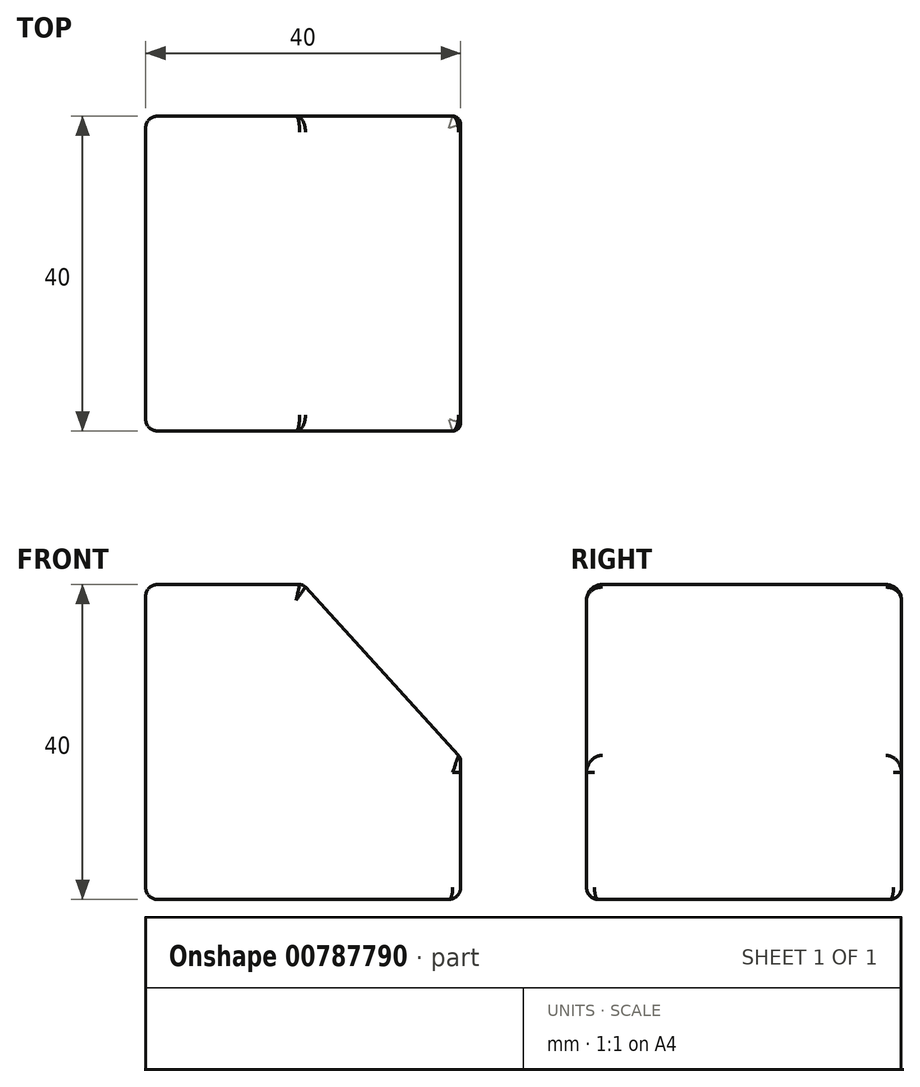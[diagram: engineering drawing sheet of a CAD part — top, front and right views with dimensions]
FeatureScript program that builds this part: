
annotation { "Feature Type Name" : "Feature", "Feature Type Description" : "" }
export const myFeature = defineFeature(function(context is Context, id is Id, definition is map)
    precondition{}
    {
        {
            var Q0;
            Q0=qCreatedBy(makeId("Front.planeOp"),FACE);
            var sketch = newSketch(context, id + "F0", { "sketchPlane" : qUnion([Q0])});
            skLineSegment(sketch, "E0", {"start": v(-35.08, 0) * mm, "end": v(-35.08, 40) * mm});
            skLineSegment(sketch, "E1", {"start": v(-35.08, 40) * mm, "end": v(-15.08, 40) * mm});
            skLineSegment(sketch, "E2", {"start": v(4.92, 0) * mm, "end": v(4.92, 0) * mm});
            skLineSegment(sketch, "E3", {"start": v(4.92, 0) * mm, "end": v(-35.08, 0) * mm});
            skLineSegment(sketch, "E4", {"start": v(-15.08, 40) * mm, "end": v(4.92, 18) * mm});
            skLineSegment(sketch, "E5", {"start": v(4.92, 18) * mm, "end": v(4.92, 0) * mm});
            skSolve(sketch);
        }
        {
            var Q0;
            Q0 = qSketchRegion(id + "F0", true);
            extrude(context, id + "F1", {"entities" : qUnion([Q0]), "depth" : 40 * mm, "offsetDistance" : 25 * mm});
        }
        {
            var Q0;
            Q0=makeQuery(id+"F1.opExtrude","CAP_EDGE",EDGE,{"disambiguationData":[OSD([sQuery(id+"F0.wireOp",EDGE,"E1")])],"isStart":false});
            var Q1;
            Q1=makeQuery(id+"F1.opExtrude","CAP_EDGE",EDGE,{"disambiguationData":[OSD([sQuery(id+"F0.wireOp",EDGE,"E4")])],"isStart":false});
            fillet(context, id + "F2", {"entities" : qUnion([Q0, Q1]), "radius" : 2 * mm, "tangentPropagation" : true, "allowEdgeOverflow" : false});
        }
        {
            var Q0;
            Q0=makeQuery(id+"F1.opExtrude","CAP_EDGE",EDGE,{"disambiguationData":[OSD([sQuery(id+"F0.wireOp",EDGE,"E4")])],"isStart":true});
            var Q1;
            Q1=makeQuery(id+"F1.opExtrude","CAP_EDGE",EDGE,{"disambiguationData":[OSD([sQuery(id+"F0.wireOp",EDGE,"E1")])],"isStart":true});
            fillet(context, id + "F3", {"entities" : qUnion([Q0, Q1]), "radius" : 2 * mm, "tangentPropagation" : true, "allowEdgeOverflow" : false});
        }
        {
            var Q0;
            Q0=makeQuery(id+"F1.opExtrude","SWEPT_EDGE",EDGE,{"disambiguationData":[OSD([sQuery(id+"F0.wireOp",EDGE,"E1"),sQuery(id+"F0.wireOp",EDGE,"E4")])]});
            fillet(context, id + "F4", {"entities" : qUnion([Q0]), "radius" : 1 * mm, "tangentPropagation" : true, "allowEdgeOverflow" : false});
        }
        {
            var Q0;
            Q0=makeQuery(id+"F1.opExtrude","SWEPT_EDGE",EDGE,{"disambiguationData":[OSD([sQuery(id+"F0.wireOp",EDGE,"E4"),sQuery(id+"F0.wireOp",EDGE,"E5")])]});
            fillet(context, id + "F5", {"entities" : qUnion([Q0]), "radius" : 1 * mm, "tangentPropagation" : true, "allowEdgeOverflow" : false});
        }
        {
            var Q0;
            Q0=makeQuery(id+"F1.opExtrude","SWEPT_FACE",FACE,{"disambiguationData":[OSD([sQuery(id+"F0.wireOp",EDGE,"E4")])]});
            var sketch = newSketch(context, id + "F6", { "sketchPlane" : qUnion([Q0])});
            skCircle(sketch, "E6", {"center": v(-19.93, 26.57) * mm, "radius": 2.5 * mm});
            skSolve(sketch);
        }
        {
            var Q0;
            Q0=sQuery(id+"F6.wireOp",EDGE,"E6");
            extrude(context, id + "F7", {"bodyType" : ToolBodyType.SURFACE, "surfaceEntities" : qUnion([Q0]), "depth" : 30 * mm, "offsetDistance" : 25 * mm});
        }
        {
            var Q0;
            Q0=makeQuery(id+"F1.opExtrude","SWEPT_FACE",FACE,{"disambiguationData":[OSD([sQuery(id+"F0.wireOp",EDGE,"E0")])]});
            var Q1;
            Q1=makeQuery(id+"F1.opExtrude","CAP_FACE",FACE,{"disambiguationData":[OSD([sQuery(id+"F0.wireOp",EDGE,"E0"),sQuery(id+"F0.wireOp",EDGE,"E1"),sQuery(id+"F0.wireOp",EDGE,"E3"),sQuery(id+"F0.wireOp",EDGE,"E4"),sQuery(id+"F0.wireOp",EDGE,"E5")])],"isStart":false});
            fillet(context, id + "F8", {"entities" : qUnion([Q0, Q1]), "radius" : 1.5 * mm, "tangentPropagation" : true, "allowEdgeOverflow" : false});
        }
    });
